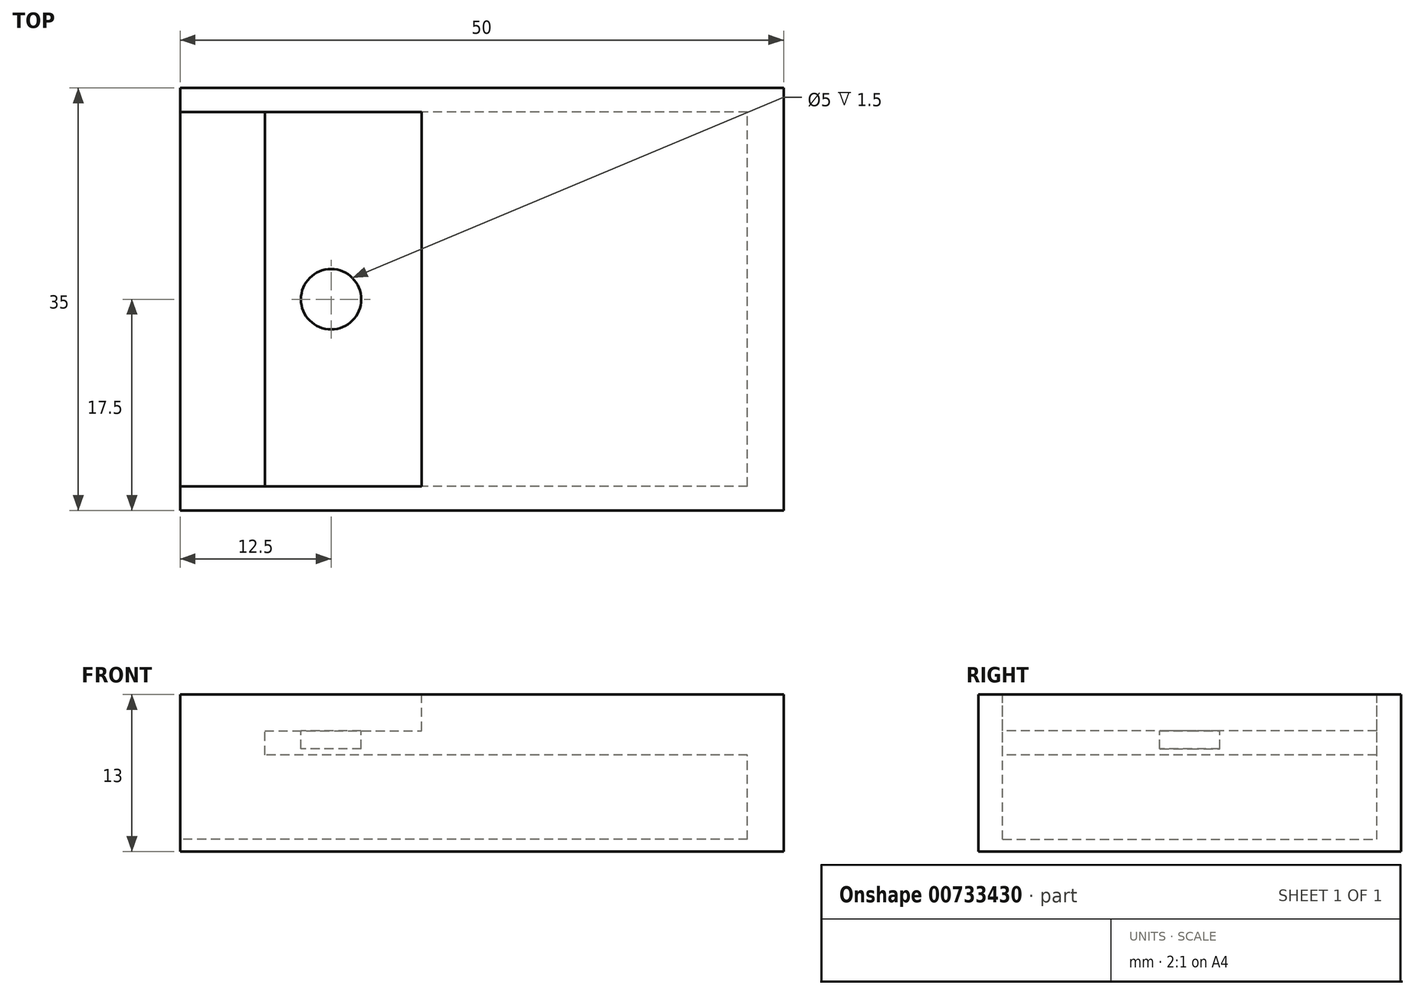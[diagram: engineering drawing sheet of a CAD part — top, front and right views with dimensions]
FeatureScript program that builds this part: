
annotation { "Feature Type Name" : "Feature", "Feature Type Description" : "" }
export const myFeature = defineFeature(function(context is Context, id is Id, definition is map)
    precondition{}
    {
        {
            var Q0;
            Q0=qCreatedBy(makeId("Top.planeOp"),FACE);
            var sketch = newSketch(context, id + "F0", { "sketchPlane" : qUnion([Q0])});
            skLineSegment(sketch, "E0.bottom", {"start": v(25, 17.5) * mm, "end": v(-25, 17.5) * mm});
            skLineSegment(sketch, "E0.top", {"start": v(25, -17.5) * mm, "end": v(-25, -17.5) * mm});
            skLineSegment(sketch, "E0.left", {"start": v(25, 17.5) * mm, "end": v(25, -17.5) * mm});
            skLineSegment(sketch, "E0.right", {"start": v(-25, 17.5) * mm, "end": v(-25, -17.5) * mm});
            skPoint(sketch, "E0.middle", {"position": v(0, 0) * mm});
            skSolve(sketch);
        }
        {
            var Q0;
            Q0=qSketchRegion(id+"F0",true);
            extrude(context, id + "F1", {"entities" : qUnion([Q0]), "depth" : 13 * mm, "offsetDistance" : 25 * mm});
        }
        {
            var Q0;
            Q0=makeQuery(id+"F1.opExtrude","SWEPT_FACE",FACE,{"disambiguationData":[OSD([sQuery(id+"F0.wireOp",EDGE,"E0.right")])]});
            var sketch = newSketch(context, id + "F2", { "sketchPlane" : qUnion([Q0])});
            skLineSegment(sketch, "E1.bottom", {"start": v(15.5, 1) * mm, "end": v(-15.5, 1) * mm});
            skLineSegment(sketch, "E1.top", {"start": v(15.5, 21) * mm, "end": v(-15.5, 21) * mm});
            skLineSegment(sketch, "E1.left", {"start": v(15.5, 1) * mm, "end": v(15.5, 21) * mm});
            skLineSegment(sketch, "E1.right", {"start": v(-15.5, 1) * mm, "end": v(-15.5, 21) * mm});
            skPoint(sketch, "E1.middle", {"position": v(0, 11) * mm});
            skSolve(sketch);
        }
        {
            var Q0;
            Q0=qSketchRegion(id+"F2",true);
            extrude(context, id + "F3", {"entities" : qUnion([Q0]), "operationType" : NewBodyOperationType.REMOVE, "oppositeDirection" : true, "depth" : 20 * mm, "offsetDistance" : 25 * mm});
        }
        {
            var Q0;
            Q0=makeQuery(id+"F3.boolean.opBoolean","COPY",FACE,{"derivedFrom":makeQuery(id+"F3.opExtrude","CAP_FACE",FACE,{"disambiguationData":[OSD([sQuery(id+"F2.wireOp",EDGE,"E1.bottom"),sQuery(id+"F2.wireOp",EDGE,"E1.top"),sQuery(id+"F2.wireOp",EDGE,"E1.left"),sQuery(id+"F2.wireOp",EDGE,"E1.right")])],"isStart":false})});
            var sketch = newSketch(context, id + "F4", { "sketchPlane" : qUnion([Q0])});
            skPoint(sketch, "E2.middle", {"position": v(0, 4.3) * mm});
            skLineSegment(sketch, "E3.bottom", {"start": v(-15.5, 1) * mm, "end": v(15.5, 1) * mm});
            skLineSegment(sketch, "E3.top", {"start": v(-15.5, 8) * mm, "end": v(15.5, 8) * mm});
            skLineSegment(sketch, "E3.left", {"start": v(-15.5, 1) * mm, "end": v(-15.5, 8) * mm});
            skLineSegment(sketch, "E3.right", {"start": v(15.5, 1) * mm, "end": v(15.5, 8) * mm});
            skSolve(sketch);
        }
        {
            var Q0;
            Q0=qSketchRegion(id+"F4",true);
            extrude(context, id + "F5", {"entities" : qUnion([Q0]), "operationType" : NewBodyOperationType.REMOVE, "oppositeDirection" : true, "depth" : 27 * mm, "offsetDistance" : 25 * mm});
        }
        {
            var Q0;
            Q0=makeQuery(id+"F3.boolean.opBoolean","COPY",FACE,{"derivedFrom":makeQuery(id+"F3.opExtrude","CAP_FACE",FACE,{"disambiguationData":[OSD([sQuery(id+"F2.wireOp",EDGE,"E1.bottom"),sQuery(id+"F2.wireOp",EDGE,"E1.top"),sQuery(id+"F2.wireOp",EDGE,"E1.left"),sQuery(id+"F2.wireOp",EDGE,"E1.right")])],"isStart":false})});
            var sketch = newSketch(context, id + "F6", { "sketchPlane" : qUnion([Q0])});
            skLineSegment(sketch, "E4.bottom", {"start": v(-15.5, 8) * mm, "end": v(15.5, 8) * mm});
            skLineSegment(sketch, "E4.top", {"start": v(-15.5, 10) * mm, "end": v(15.5, 10) * mm});
            skLineSegment(sketch, "E4.left", {"start": v(-15.5, 8) * mm, "end": v(-15.5, 10) * mm});
            skLineSegment(sketch, "E4.right", {"start": v(15.5, 8) * mm, "end": v(15.5, 10) * mm});
            skSolve(sketch);
        }
        {
            var Q0;
            Q0 = qSketchRegion(id + "F6", true);
            extrude(context, id + "F7", {"entities" : qUnion([Q0]), "operationType" : NewBodyOperationType.ADD, "depth" : 13 * mm, "offsetDistance" : 25 * mm});
        }
        {
            var Q0;
            Q0=makeQuery(id+"F7.opExtrude","SWEPT_FACE",FACE,{"disambiguationData":[OSD([sQuery(id+"F6.wireOp",EDGE,"E4.top")])]});
            var sketch = newSketch(context, id + "F8", { "sketchPlane" : qUnion([Q0])});
            skCircle(sketch, "E5", {"center": v(-12.5, 0) * mm, "radius": 2.5 * mm});
            skSolve(sketch);
        }
        {
            var Q0;
            Q0=makeQuery(id+"F8.imprint","IMPRINT",FACE,{"disambiguationData":[TD([[makeQuery(id+"F8.imprint","IMPRINT",EDGE,{"derivedFrom":sQuery(id+"F8.wireOp",EDGE,"E5")}),1.0]])]});
            extrude(context, id + "F9", {"entities" : qUnion([Q0]), "operationType" : NewBodyOperationType.REMOVE, "oppositeDirection" : true, "depth" : 1.5 * mm, "offsetDistance" : 25 * mm});
        }
    });
